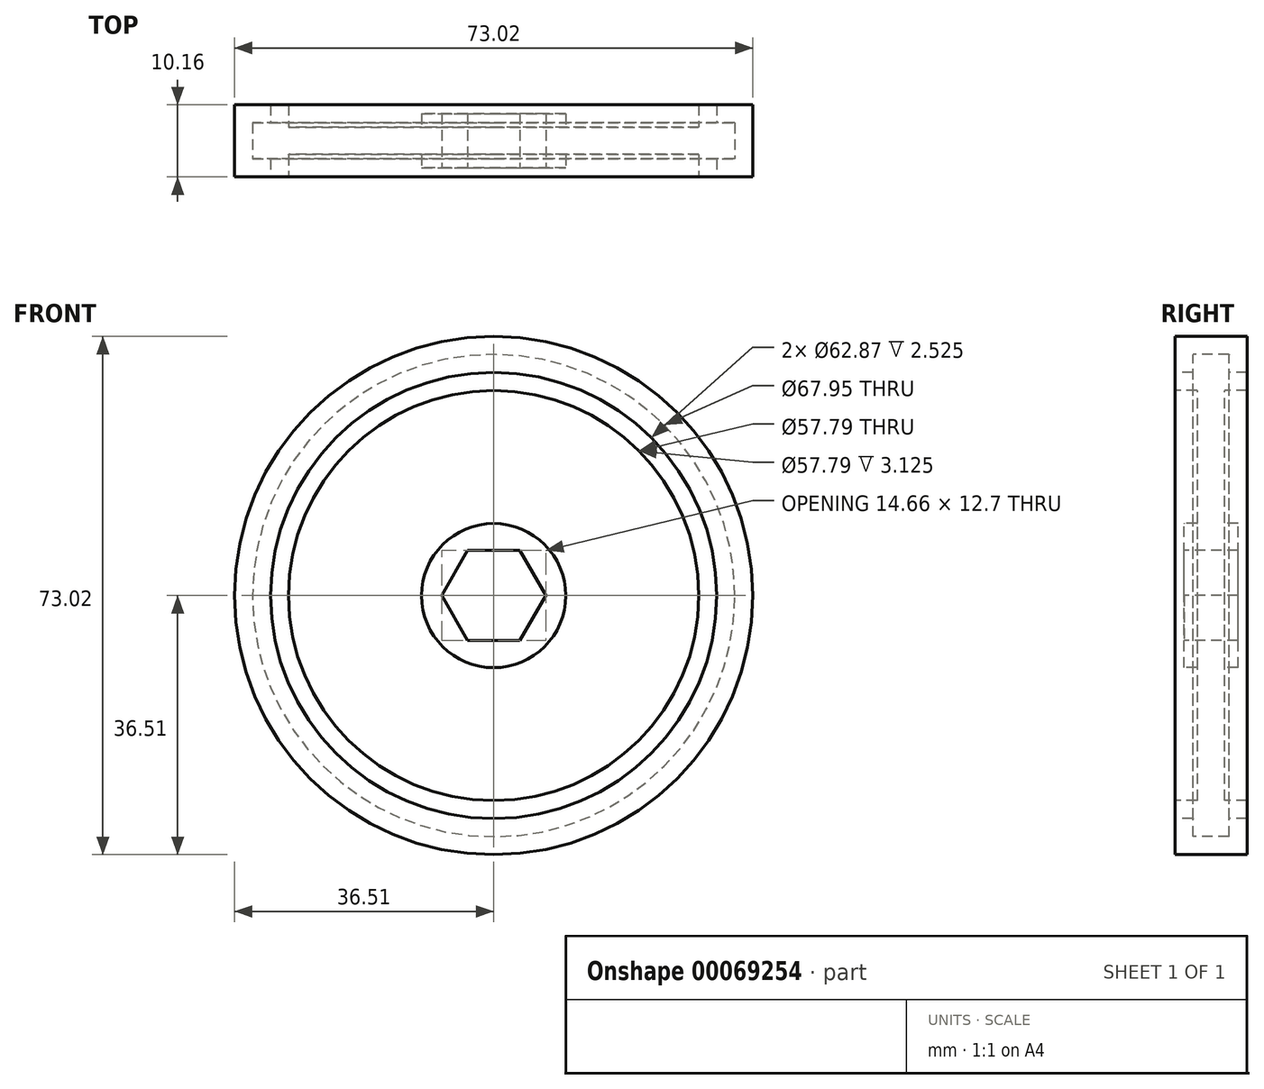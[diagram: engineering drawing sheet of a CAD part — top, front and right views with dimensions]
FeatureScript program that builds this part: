
annotation { "Feature Type Name" : "Feature", "Feature Type Description" : "" }
export const myFeature = defineFeature(function(context is Context, id is Id, definition is map)
    precondition{}
    {
        {
            var Q0;
            Q0=qCreatedBy(makeId("Top.planeOp"),FACE);
            var sketch = newSketch(context, id + "F0", { "sketchPlane" : qUnion([Q0])});
            skLineSegment(sketch, "E0.bottom", {"start": v(0, 0) * mm, "end": v(10.16, 0) * mm});
            skLineSegment(sketch, "E0.top", {"start": v(0, 3.8) * mm, "end": v(10.16, 3.8) * mm});
            skLineSegment(sketch, "E0.left", {"start": v(0, 0) * mm, "end": v(0, 3.8) * mm});
            skLineSegment(sketch, "E0.right", {"start": v(10.16, 0) * mm, "end": v(10.16, 3.8) * mm});
            skLineSegment(sketch, "E1.bottom", {"start": v(10.16, 0) * mm, "end": v(28.9, 0) * mm});
            skLineSegment(sketch, "E1.top", {"start": v(10.16, 1.9) * mm, "end": v(28.9, 1.9) * mm});
            skLineSegment(sketch, "E1.left", {"start": v(10.16, 0) * mm, "end": v(10.16, 1.9) * mm});
            skLineSegment(sketch, "E1.right", {"start": v(28.9, 0) * mm, "end": v(28.9, 1.9) * mm});
            skLineSegment(sketch, "E2.bottom", {"start": v(28.9, 0) * mm, "end": v(31.43, 0) * mm});
            skLineSegment(sketch, "E2.top", {"start": v(28.9, 5.08) * mm, "end": v(31.43, 5.08) * mm});
            skLineSegment(sketch, "E2.left", {"start": v(28.9, 0) * mm, "end": v(28.9, 5.08) * mm});
            skLineSegment(sketch, "E2.right", {"start": v(31.43, 0) * mm, "end": v(31.43, 5.08) * mm});
            skLineSegment(sketch, "E3.bottom", {"start": v(31.43, 2.54) * mm, "end": v(33.97, 2.54) * mm});
            skLineSegment(sketch, "E3.top", {"start": v(31.43, 0) * mm, "end": v(33.97, 0) * mm});
            skLineSegment(sketch, "E3.left", {"start": v(31.43, 2.54) * mm, "end": v(31.43, 0) * mm});
            skLineSegment(sketch, "E3.right", {"start": v(33.97, 2.54) * mm, "end": v(33.97, 0) * mm});
            skLineSegment(sketch, "E4.MirrorCS", {"start": v(28.9, 0) * mm, "end": v(28.9, -1.9) * mm});
            skLineSegment(sketch, "E5.MirrorCS", {"start": v(31.43, -2.54) * mm, "end": v(31.43, 0) * mm});
            skLineSegment(sketch, "E6.MirrorCS", {"start": v(31.43, -2.54) * mm, "end": v(33.97, -2.54) * mm});
            skLineSegment(sketch, "E7.MirrorCS", {"start": v(31.43, 0) * mm, "end": v(31.43, -5.08) * mm});
            skLineSegment(sketch, "E8.MirrorCS", {"start": v(28.9, 0) * mm, "end": v(28.9, -5.08) * mm});
            skLineSegment(sketch, "E9.MirrorCS", {"start": v(33.97, -2.54) * mm, "end": v(33.97, 0) * mm});
            skLineSegment(sketch, "E10.MirrorCS", {"start": v(0, -3.8) * mm, "end": v(10.16, -3.8) * mm});
            skLineSegment(sketch, "E11.MirrorCS", {"start": v(0, 0) * mm, "end": v(0, -3.8) * mm});
            skLineSegment(sketch, "E12.MirrorCS", {"start": v(10.16, 0) * mm, "end": v(10.16, -1.9) * mm});
            skLineSegment(sketch, "E13.MirrorCS", {"start": v(10.16, -1.9) * mm, "end": v(28.9, -1.9) * mm});
            skLineSegment(sketch, "E14.MirrorCS", {"start": v(28.9, -5.08) * mm, "end": v(31.43, -5.08) * mm});
            skLineSegment(sketch, "E15.MirrorCS", {"start": v(10.16, 0) * mm, "end": v(10.16, -3.8) * mm});
            skSolve(sketch);
        }
        {
            var Q0;
            Q0=makeQuery(id+"F0.imprint","IMPRINT",FACE,{"disambiguationData":[TD([[makeQuery(id+"F0.imprint","IMPRINT",EDGE,{"derivedFrom":sQuery(id+"F0.wireOp",EDGE,"E0.bottom")}),1.0]])]});
            var Q1;
            {var subQ0=sQuery(id+"F0.wireOp",EDGE,"E1.top");Q1=makeQuery(id+"F0.imprint","IMPRINT",FACE,{"disambiguationData":[TD([[makeQuery(id+"F0.imprint","IMPRINT",EDGE,{"derivedFrom":subQ0}),-1.0]])]});}
            var Q2;
            {var subQ1=sQuery(id+"F0.wireOp",EDGE,"E0.bottom");Q2=makeQuery(id+"F0.imprint","IMPRINT",FACE,{"disambiguationData":[TD([[makeQuery(id+"F0.imprint","IMPRINT",EDGE,{"derivedFrom":subQ1}),-1.0]])]});}
            var Q3;
            {var subQ2=sQuery(id+"F0.wireOp",EDGE,"E13.MirrorCS");Q3=makeQuery(id+"F0.imprint","IMPRINT",FACE,{"disambiguationData":[TD([[makeQuery(id+"F0.imprint","IMPRINT",EDGE,{"derivedFrom":subQ2}),1.0]])]});}
            var Q4;
            {var subQ0=sQuery(id+"F0.wireOp",EDGE,"E6.MirrorCS");Q4=makeQuery(id+"F0.imprint","IMPRINT",FACE,{"disambiguationData":[TD([[makeQuery(id+"F0.imprint","IMPRINT",EDGE,{"derivedFrom":subQ0}),1.0]])]});}
            var Q5;
            Q5=makeQuery(id+"F0.imprint","IMPRINT",FACE,{"disambiguationData":[TD([[makeQuery(id+"F0.imprint","IMPRINT",EDGE,{"derivedFrom":sQuery(id+"F0.wireOp",EDGE,"E3.bottom")}),-1.0]])]});
            var Q6;
            {var subQ2=sQuery(id+"F0.wireOp",EDGE,"E2.top");Q6=makeQuery(id+"F0.imprint","IMPRINT",FACE,{"disambiguationData":[TD([[makeQuery(id+"F0.imprint","IMPRINT",EDGE,{"derivedFrom":subQ2}),-1.0]])]});}
            var Q7;
            {var subQ1=sQuery(id+"F0.wireOp",EDGE,"E2.bottom");Q7=makeQuery(id+"F0.imprint","IMPRINT",FACE,{"disambiguationData":[TD([[makeQuery(id+"F0.imprint","IMPRINT",EDGE,{"derivedFrom":subQ1}),-1.0]])]});}
            var Q8;
            Q8=sQuery(id+"F0.wireOp",EDGE,"E0.left");
            revolve(context, id + "F1", {"entities" : qUnion([Q0, Q1, Q2, Q3, Q4, Q5, Q6, Q7]), "axis" : qUnion([Q8]), "revolveType" : RevolveType.FULL});
        }
        {
            var Q0;
            Q0=makeQuery(id+"F1.opRevolve","SWEPT_FACE",FACE,{"disambiguationData":[OSD([sQuery(id+"F0.wireOp",EDGE,"E10.MirrorCS")])]});
            var sketch = newSketch(context, id + "F2", { "sketchPlane" : qUnion([Q0])});
            skPoint(sketch, "E16.0", {"position": v(0, 0) * mm});
            skCircle(sketch, "E17.cCircle", {"center": v(0, 0) * mm, "radius": 6.35 * mm, "construction": true});
            skLineSegment(sketch, "E17.0", {"start": v(-3.67, 6.35) * mm, "end": v(3.67, 6.35) * mm});
            skLineSegment(sketch, "E17.1", {"start": v(3.67, 6.35) * mm, "end": v(7.33, 0) * mm});
            skLineSegment(sketch, "E17.2", {"start": v(7.33, 0) * mm, "end": v(3.67, -6.35) * mm});
            skLineSegment(sketch, "E17.3", {"start": v(3.67, -6.35) * mm, "end": v(-3.67, -6.35) * mm});
            skLineSegment(sketch, "E17.4", {"start": v(-3.67, -6.35) * mm, "end": v(-7.33, 0) * mm});
            skLineSegment(sketch, "E17.5", {"start": v(-7.33, 0) * mm, "end": v(-3.67, 6.35) * mm});
            skPoint(sketch, "E17.0.midPoint", {"position": v(0, 6.35) * mm});
            skSolve(sketch);
        }
        {
            var Q0;
            Q0=makeQuery(id+"F2.imprint","IMPRINT",FACE,{"disambiguationData":[TD([[makeQuery(id+"F2.imprint","IMPRINT",EDGE,{"derivedFrom":sQuery(id+"F2.wireOp",EDGE,"E17.0")}),-1.0]])]});
            extrude(context, id + "F3", {"entities" : qUnion([Q0]), "operationType" : NewBodyOperationType.REMOVE, "endBound" : BoundingType.THROUGH_ALL, "oppositeDirection" : true, "depth" : 25.4 * mm});
        }
        {
            var Q0;
            Q0=qCreatedBy(makeId("Top.planeOp"),FACE);
            var sketch = newSketch(context, id + "F4", { "sketchPlane" : qUnion([Q0])});
            skLineSegment(sketch, "E18.0", {"start": v(31.43, 0) * mm, "end": v(31.43, 5.08) * mm});
            skLineSegment(sketch, "E19.0", {"start": v(31.43, 2.54) * mm, "end": v(33.97, 2.54) * mm});
            skLineSegment(sketch, "E20.0", {"start": v(33.97, 2.54) * mm, "end": v(33.97, 0) * mm});
            skLineSegment(sketch, "E21.0", {"start": v(33.97, -2.54) * mm, "end": v(33.97, 0) * mm});
            skLineSegment(sketch, "E22.0", {"start": v(31.43, -2.54) * mm, "end": v(33.97, -2.54) * mm});
            skLineSegment(sketch, "E23.0", {"start": v(31.43, 0) * mm, "end": v(31.43, -5.08) * mm});
            skLineSegment(sketch, "E24", {"start": v(31.43, 5.08) * mm, "end": v(36.51, 5.08) * mm});
            skLineSegment(sketch, "E25", {"start": v(36.51, 5.08) * mm, "end": v(36.51, -5.08) * mm});
            skLineSegment(sketch, "E26", {"start": v(36.51, -5.08) * mm, "end": v(31.43, -5.08) * mm});
            skSolve(sketch);
        }
        {
            var Q0;
            {var subQ2=sQuery(id+"F4.wireOp",EDGE,"E19.0");Q0=makeQuery(id+"F4.imprint","IMPRINT",FACE,{"disambiguationData":[TD([[makeQuery(id+"F4.imprint","IMPRINT",EDGE,{"derivedFrom":subQ2}),1.0]])]});}
            var Q1;
            Q1=sQuery(id+"F0.wireOp",EDGE,"E0.left");
            revolve(context, id + "F5", {"entities" : qUnion([Q0]), "axis" : qUnion([Q1]), "revolveType" : RevolveType.FULL});
        }
        {
            assignVariable(context, id + "F6", {"name" : "fillet_a", "anyValue" : 0.05});
        }
        {
            assignVariable(context, id + "F7", {"name" : "fillet_b", "anyValue" : 0.01});
        }
        {
            var Q0;
            Q0=makeQuery(id+"F1.opRevolve","SWEPT_EDGE",EDGE,{"disambiguationData":[OSD([sQuery(id+"F0.wireOp",EDGE,"E8.MirrorCS"),sQuery(id+"F0.wireOp",EDGE,"E13.MirrorCS")])]});
            var Q1;
            Q1=makeQuery(id+"F1.opRevolve","SWEPT_EDGE",EDGE,{"disambiguationData":[OSD([sQuery(id+"F0.wireOp",EDGE,"E13.MirrorCS"),sQuery(id+"F0.wireOp",EDGE,"E15.MirrorCS")])]});
            var Q2;
            Q2=makeQuery(id+"F1.opRevolve","SWEPT_EDGE",EDGE,{"disambiguationData":[OSD([sQuery(id+"F0.wireOp",EDGE,"E1.top"),sQuery(id+"F0.wireOp",EDGE,"E2.left")])]});
            var Q3;
            Q3=makeQuery(id+"F1.opRevolve","SWEPT_EDGE",EDGE,{"disambiguationData":[OSD([sQuery(id+"F0.wireOp",EDGE,"E0.right"),sQuery(id+"F0.wireOp",EDGE,"E1.top"),sQuery(id+"F0.wireOp",EDGE,"E1.left")])]});
            fillet(context, id + "F8", {"entities" : qUnion([Q0, Q1, Q2, Q3]), "radius" : (getVariable(context, 'fillet_a')) * mm, "tangentPropagation" : true, "allowEdgeOverflow" : false});
        }
        {
            var Q0;
            Q0=makeQuery(id+"F1.opRevolve","SWEPT_EDGE",EDGE,{"disambiguationData":[OSD([sQuery(id+"F0.wireOp",EDGE,"E8.MirrorCS"),sQuery(id+"F0.wireOp",EDGE,"E14.MirrorCS")])]});
            var Q1;
            Q1=makeQuery(id+"F1.opRevolve","SWEPT_EDGE",EDGE,{"disambiguationData":[OSD([sQuery(id+"F0.wireOp",EDGE,"E10.MirrorCS"),sQuery(id+"F0.wireOp",EDGE,"E15.MirrorCS")])]});
            fillet(context, id + "F9", {"entities" : qUnion([Q0, Q1]), "radius" : (getVariable(context, 'fillet_b')) * mm, "tangentPropagation" : true, "allowEdgeOverflow" : false});
        }
        {
            var Q0;
            Q0=makeQuery(id+"F1.opRevolve","SWEPT_EDGE",EDGE,{"disambiguationData":[OSD([sQuery(id+"F0.wireOp",EDGE,"E6.MirrorCS"),sQuery(id+"F0.wireOp",EDGE,"E7.MirrorCS")])]});
            var Q1;
            Q1=makeQuery(id+"F1.opRevolve","SWEPT_EDGE",EDGE,{"disambiguationData":[OSD([sQuery(id+"F0.wireOp",EDGE,"E6.MirrorCS"),sQuery(id+"F0.wireOp",EDGE,"E9.MirrorCS")])]});
            var Q2;
            Q2=makeQuery(id+"F1.opRevolve","SWEPT_EDGE",EDGE,{"disambiguationData":[OSD([sQuery(id+"F0.wireOp",EDGE,"E2.right"),sQuery(id+"F0.wireOp",EDGE,"E3.bottom"),sQuery(id+"F0.wireOp",EDGE,"E3.left")])]});
            var Q3;
            Q3=makeQuery(id+"F1.opRevolve","SWEPT_EDGE",EDGE,{"disambiguationData":[OSD([sQuery(id+"F0.wireOp",EDGE,"E3.bottom"),sQuery(id+"F0.wireOp",EDGE,"E3.right")])]});
            fillet(context, id + "F10", {"entities" : qUnion([Q0, Q1, Q2, Q3]), "radius" : (getVariable(context, 'fillet_b')) * mm, "tangentPropagation" : true, "allowEdgeOverflow" : false});
        }
        {
            var Q0;
            Q0=makeQuery(id+"F5.opRevolve","SWEPT_EDGE",EDGE,{"disambiguationData":[OSD([sQuery(id+"F4.wireOp",EDGE,"E19.0"),sQuery(id+"F4.wireOp",EDGE,"E20.0")])]});
            var Q1;
            Q1=makeQuery(id+"F5.opRevolve","SWEPT_EDGE",EDGE,{"disambiguationData":[OSD([sQuery(id+"F4.wireOp",EDGE,"E18.0"),sQuery(id+"F4.wireOp",EDGE,"E19.0")])]});
            var Q2;
            Q2=makeQuery(id+"F5.opRevolve","SWEPT_EDGE",EDGE,{"disambiguationData":[OSD([sQuery(id+"F4.wireOp",EDGE,"E22.0"),sQuery(id+"F4.wireOp",EDGE,"E23.0")])]});
            var Q3;
            Q3=makeQuery(id+"F5.opRevolve","SWEPT_EDGE",EDGE,{"disambiguationData":[OSD([sQuery(id+"F4.wireOp",EDGE,"E21.0"),sQuery(id+"F4.wireOp",EDGE,"E22.0")])]});
            fillet(context, id + "F11", {"entities" : qUnion([Q0, Q1, Q2, Q3]), "radius" : (getVariable(context, 'fillet_b')) * mm, "tangentPropagation" : true, "allowEdgeOverflow" : false});
        }
    });
